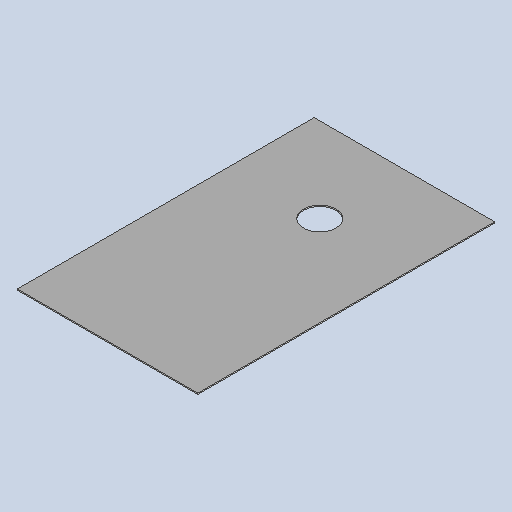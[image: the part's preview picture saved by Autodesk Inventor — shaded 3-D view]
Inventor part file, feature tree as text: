
AUTODESK INVENTOR PART (.ipt)
format: ipt  version: 2025 (Build 290162010, 162A)  size: 248,320 bytes
history: native  units: mm
features: other x5, sketch x3, sheet_metal_op x1
ambient origin geometry x8: Origin, YZ Plane, XZ Plane, XY Plane, X Axis, Y Axis, Z Axis, Center Point
bodies: Solid1 (feature_tree)
feature tree (9):
  sheet_metal_op  "Face1"
  sketch  "Sketch2"  dims[d1=806.0mm]
  other  "A-Side Definition"
  other  "Mark3"
  sketch  "Sketch1"  dims[d0=490.0mm]
  other  "Plate1"
  sketch  "Sketch6"  dims[d2=3.0mm d8=200.0mm d9=20.0mm d10=20.0mm d11=20.0mm d42=89.0mm d43=3.0mm d44=0.0mm]
  other  "Cut1"
  other  "Definition1"
